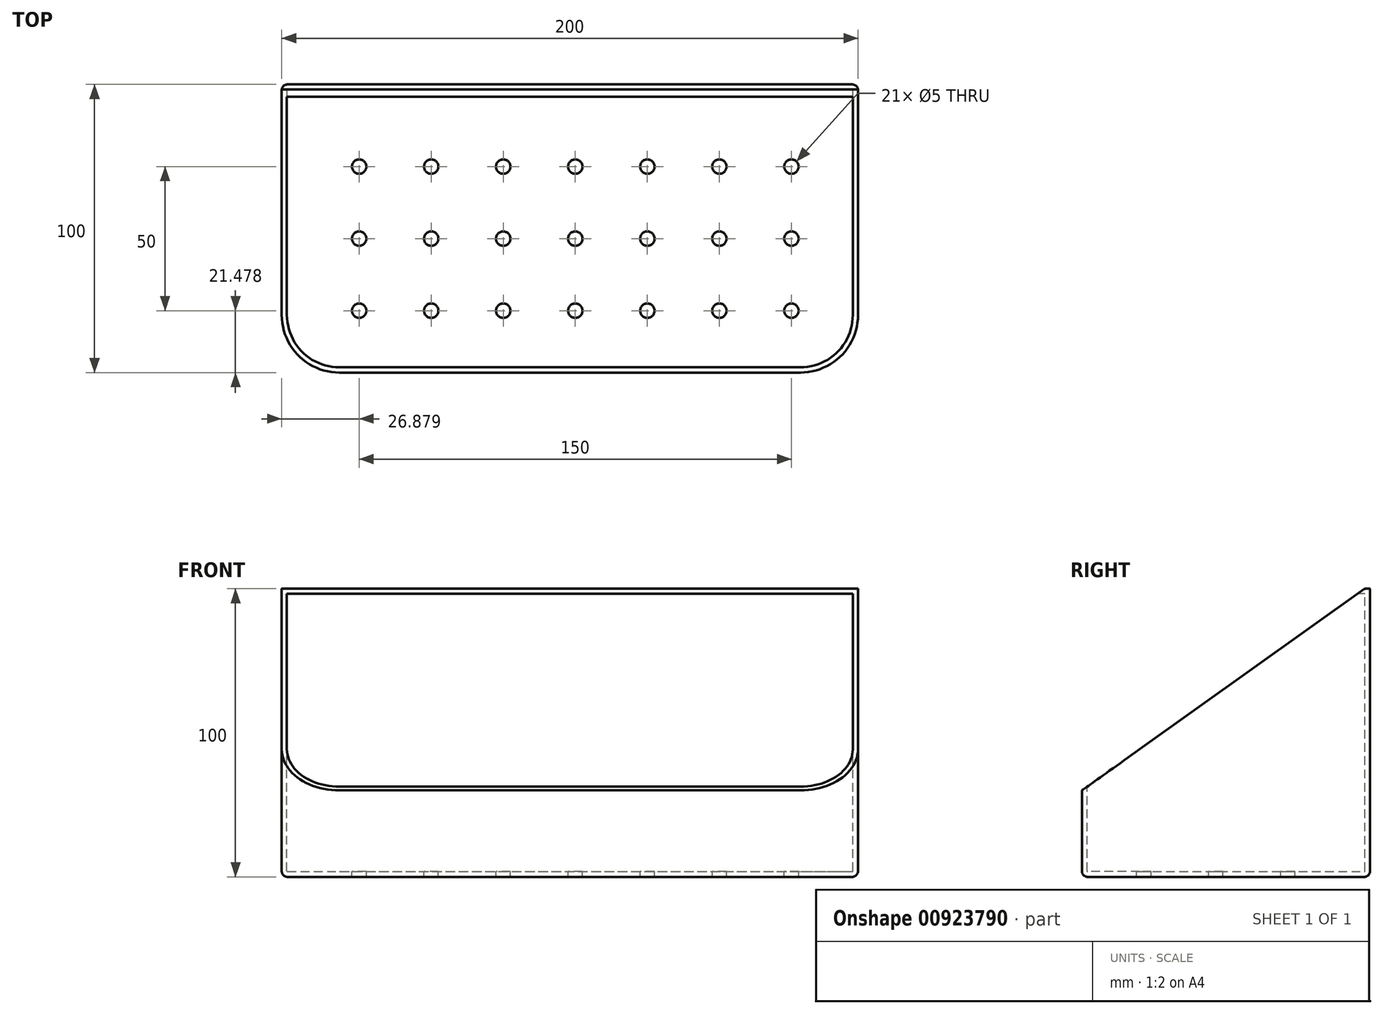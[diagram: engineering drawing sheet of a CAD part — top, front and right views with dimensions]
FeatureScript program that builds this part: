
annotation { "Feature Type Name" : "Feature", "Feature Type Description" : "" }
export const myFeature = defineFeature(function(context is Context, id is Id, definition is map)
    precondition{}
    {
        {
            var Q0;
            Q0=qCreatedBy(makeId("Top.planeOp"),FACE);
            var sketch = newSketch(context, id + "F0", { "sketchPlane" : qUnion([Q0])});
            skLineSegment(sketch, "E0.bottom", {"start": v(0, 0) * mm, "end": v(200, 0) * mm});
            skLineSegment(sketch, "E0.top", {"start": v(0, 100) * mm, "end": v(200, 100) * mm});
            skLineSegment(sketch, "E0.left", {"start": v(0, 0) * mm, "end": v(0, 100) * mm});
            skLineSegment(sketch, "E0.right", {"start": v(200, 0) * mm, "end": v(200, 100) * mm});
            skSolve(sketch);
        }
        {
            var Q0;
            Q0=makeQuery(id+"F0.imprint","IMPRINT",FACE,{"disambiguationData":[TD([[makeQuery(id+"F0.imprint","IMPRINT",EDGE,{"derivedFrom":sQuery(id+"F0.wireOp",EDGE,"E0.bottom")}),1.0]])]});
            extrude(context, id + "F1", {"entities" : qUnion([Q0]), "depth" : 100 * mm, "offsetDistance" : 25 * mm});
        }
        {
            var Q0;
            Q0=makeQuery(id+"F1.opExtrude","SWEPT_FACE",FACE,{"disambiguationData":[OSD([sQuery(id+"F0.wireOp",EDGE,"E0.right")])]});
            var sketch = newSketch(context, id + "F2", { "sketchPlane" : qUnion([Q0])});
            skLineSegment(sketch, "E1", {"start": v(98.2, 100) * mm, "end": v(0, 30) * mm});
            skLineSegment(sketch, "E2", {"start": v(0, 30) * mm, "end": v(0, 100) * mm});
            skLineSegment(sketch, "E3", {"start": v(0, 100) * mm, "end": v(98.2, 100) * mm});
            skSolve(sketch);
        }
        {
            var Q0;
            Q0=makeQuery(id+"F2.imprint","IMPRINT",FACE,{"disambiguationData":[TD([[makeQuery(id+"F2.imprint","IMPRINT",EDGE,{"derivedFrom":sQuery(id+"F2.wireOp",EDGE,"E1")}),-1.0]])]});
            extrude(context, id + "F3", {"entities" : qUnion([Q0]), "operationType" : NewBodyOperationType.REMOVE, "endBound" : BoundingType.UP_TO_NEXT, "oppositeDirection" : true, "depth" : 25 * mm, "offsetDistance" : 25 * mm});
        }
        {
            var Q0;
            Q0=makeQuery(id+"F1.opExtrude","SWEPT_EDGE",EDGE,{"disambiguationData":[OSD([sQuery(id+"F0.wireOp",EDGE,"E0.bottom"),sQuery(id+"F0.wireOp",EDGE,"E0.right")])]});
            var Q1;
            Q1=makeQuery(id+"F1.opExtrude","SWEPT_EDGE",EDGE,{"disambiguationData":[OSD([sQuery(id+"F0.wireOp",EDGE,"E0.bottom"),sQuery(id+"F0.wireOp",EDGE,"E0.left")])]});
            fillet(context, id + "F4", {"entities" : qUnion([Q0, Q1]), "radius" : 20 * mm, "tangentPropagation" : true, "allowEdgeOverflow" : false});
        }
        {
            var Q0;
            Q0=makeQuery(id+"F1.opExtrude","CAP_FACE",FACE,{"disambiguationData":[OSD([sQuery(id+"F0.wireOp",EDGE,"E0.bottom"),sQuery(id+"F0.wireOp",EDGE,"E0.top"),sQuery(id+"F0.wireOp",EDGE,"E0.left"),sQuery(id+"F0.wireOp",EDGE,"E0.right")])],"isStart":true});
            var Q1;
            Q1=makeQuery(id+"F1.opExtrude","SWEPT_EDGE",EDGE,{"disambiguationData":[OSD([sQuery(id+"F0.wireOp",EDGE,"E0.top"),sQuery(id+"F0.wireOp",EDGE,"E0.left")])]});
            var Q2;
            Q2=makeQuery(id+"F1.opExtrude","SWEPT_EDGE",EDGE,{"disambiguationData":[OSD([sQuery(id+"F0.wireOp",EDGE,"E0.top"),sQuery(id+"F0.wireOp",EDGE,"E0.right")])]});
            fillet(context, id + "F5", {"entities" : qUnion([Q0, Q1, Q2]), "radius" : 2 * mm, "tangentPropagation" : true, "allowEdgeOverflow" : false});
        }
        {
            var Q0;
            Q0=makeQuery(id+"F3.boolean.opBoolean","COPY",FACE,{"derivedFrom":makeQuery(id+"F3.opExtrude","SWEPT_FACE",FACE,{"disambiguationData":[OSD([sQuery(id+"F2.wireOp",EDGE,"E1")])]})});
            shell(context, id + "F6", {"entities" : qUnion([Q0]), "thickness" : 1.8 * mm});
        }
        {
            var Q0;
            {var subQ0=sQuery(id+"F0.wireOp",EDGE,"E0.right");var subQ1=sQuery(id+"F0.wireOp",EDGE,"E0.left");var subQ2=sQuery(id+"F0.wireOp",EDGE,"E0.top");var subQ3=sQuery(id+"F0.wireOp",EDGE,"E0.bottom");Q0=makeQuery(id+"F6.opShell","OFFSET_FACE",FACE,{"disambiguationData":[OSD([subQ3,subQ2,subQ1,subQ0]),TDD([makeQuery(id+"F1.opExtrude","CAP_FACE",FACE,{"disambiguationData":[OSD([subQ3,subQ2,subQ1,subQ0])],"isStart":true})])]});}
            var sketch = newSketch(context, id + "F7", { "sketchPlane" : qUnion([Q0])});
            skCircle(sketch, "E4", {"center": v(26.88, 21.48) * mm, "radius": 2.5 * mm});
            skCircle(sketch, "E5.0.1.0", {"center": v(26.88, 46.48) * mm, "radius": 2.5 * mm});
            skCircle(sketch, "E5.0.2.0", {"center": v(26.88, 71.48) * mm, "radius": 2.5 * mm});
            skCircle(sketch, "E5.1.0.0", {"center": v(51.88, 21.48) * mm, "radius": 2.5 * mm});
            skCircle(sketch, "E5.1.1.0", {"center": v(51.88, 46.48) * mm, "radius": 2.5 * mm});
            skCircle(sketch, "E5.1.2.0", {"center": v(51.88, 71.48) * mm, "radius": 2.5 * mm});
            skCircle(sketch, "E5.2.0.0", {"center": v(76.88, 21.48) * mm, "radius": 2.5 * mm});
            skCircle(sketch, "E5.2.1.0", {"center": v(76.88, 46.48) * mm, "radius": 2.5 * mm});
            skCircle(sketch, "E5.2.2.0", {"center": v(76.88, 71.48) * mm, "radius": 2.5 * mm});
            skCircle(sketch, "E5.3.0.0", {"center": v(101.88, 21.48) * mm, "radius": 2.5 * mm});
            skCircle(sketch, "E5.3.1.0", {"center": v(101.88, 46.48) * mm, "radius": 2.5 * mm});
            skCircle(sketch, "E5.3.2.0", {"center": v(101.88, 71.48) * mm, "radius": 2.5 * mm});
            skCircle(sketch, "E5.4.0.0", {"center": v(126.88, 21.48) * mm, "radius": 2.5 * mm});
            skCircle(sketch, "E5.4.1.0", {"center": v(126.88, 46.48) * mm, "radius": 2.5 * mm});
            skCircle(sketch, "E5.4.2.0", {"center": v(126.88, 71.48) * mm, "radius": 2.5 * mm});
            skCircle(sketch, "E5.5.0.0", {"center": v(151.88, 21.48) * mm, "radius": 2.5 * mm});
            skCircle(sketch, "E5.5.1.0", {"center": v(151.88, 46.48) * mm, "radius": 2.5 * mm});
            skCircle(sketch, "E5.5.2.0", {"center": v(151.88, 71.48) * mm, "radius": 2.5 * mm});
            skCircle(sketch, "E5.6.0.0", {"center": v(176.88, 21.48) * mm, "radius": 2.5 * mm});
            skCircle(sketch, "E5.6.1.0", {"center": v(176.88, 46.48) * mm, "radius": 2.5 * mm});
            skCircle(sketch, "E5.6.2.0", {"center": v(176.88, 71.48) * mm, "radius": 2.5 * mm});
            skLineSegment(sketch, "E5.direction1", {"start": v(26.88, 21.48) * mm, "end": v(51.88, 21.48) * mm, "construction": true});
            skLineSegment(sketch, "E5.direction2", {"start": v(26.88, 21.48) * mm, "end": v(26.88, 46.48) * mm, "construction": true});
            skSolve(sketch);
        }
        {
            var Q0;
            Q0 = qSketchRegion(id + "F7", true);
            extrude(context, id + "F8", {"entities" : qUnion([Q0]), "operationType" : NewBodyOperationType.REMOVE, "endBound" : BoundingType.UP_TO_NEXT, "oppositeDirection" : true, "depth" : 25 * mm, "offsetDistance" : 25 * mm});
        }
    });
